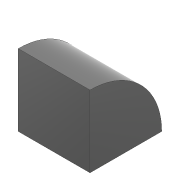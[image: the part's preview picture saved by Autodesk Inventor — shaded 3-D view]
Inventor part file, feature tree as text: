
AUTODESK INVENTOR PART (.ipt)
format: ipt  version: 2020 (Build 240168000, 168)  size: 87,040 bytes
history: native  units: mm
features: extrude x1, fillet x1, sketch x1
ambient origin geometry x8: Origin, YZ Plane, XZ Plane, XY Plane, X Axis, Y Axis, Z Axis, Center Point
bodies: Volumenkörper1 (feature_tree)
feature tree (3):
  extrude  "Extrusion1"  Depth=8.0mm
  fillet  "Rundung2"  Radius=8.0mm
  sketch  "Skizze1"  dims[d0=8.0mm d1=8.0mm d2=8.0mm d3=0.0mm d5=8.0mm]
